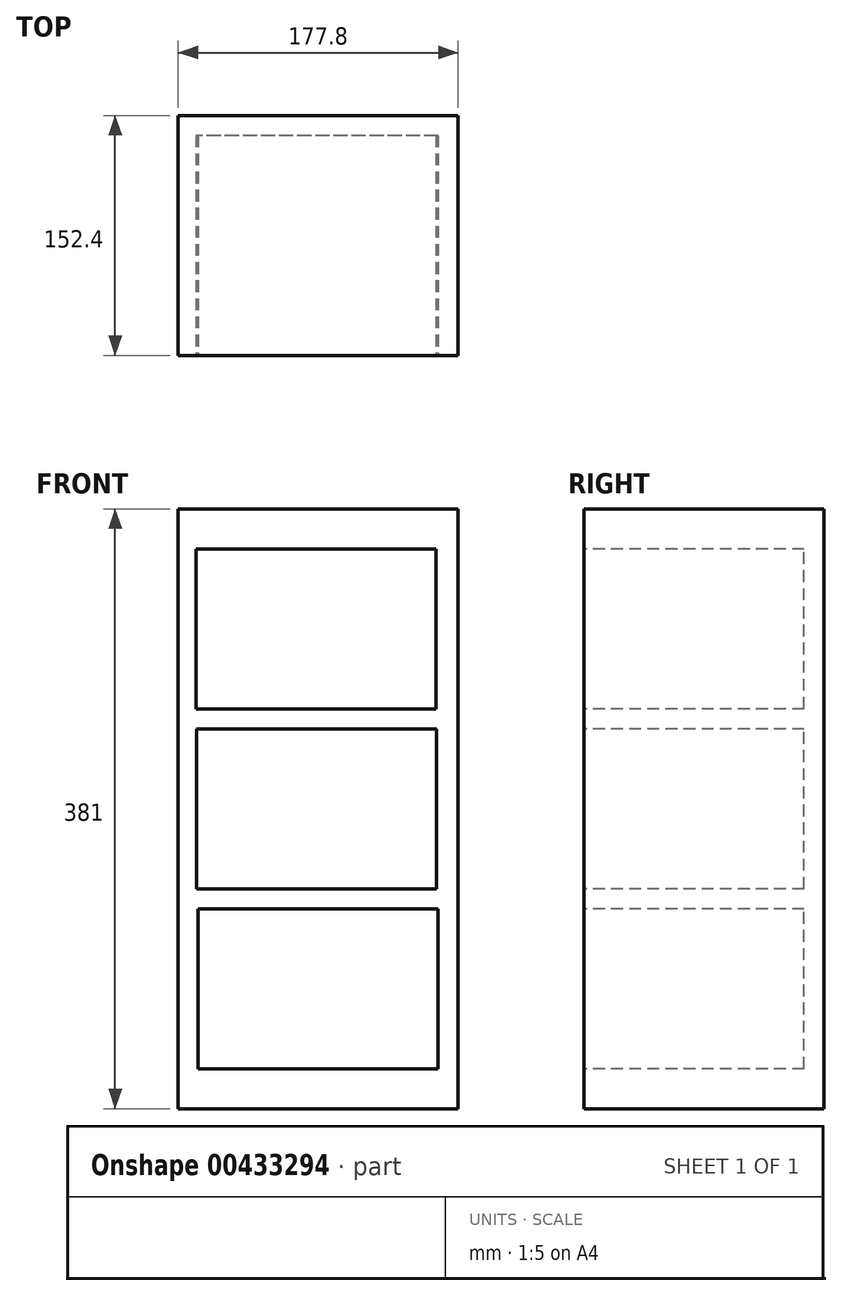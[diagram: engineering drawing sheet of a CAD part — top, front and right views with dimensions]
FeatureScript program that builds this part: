
annotation { "Feature Type Name" : "Feature", "Feature Type Description" : "" }
export const myFeature = defineFeature(function(context is Context, id is Id, definition is map)
    precondition{}
    {
        {
            var Q0;
            Q0=qCreatedBy(makeId("Top.planeOp"),FACE);
            var sketch = newSketch(context, id + "F0", { "sketchPlane" : qUnion([Q0])});
            skLineSegment(sketch, "E0.bottom", {"start": v(88.9, -76.2) * mm, "end": v(-88.9, -76.2) * mm});
            skLineSegment(sketch, "E0.top", {"start": v(88.9, 76.2) * mm, "end": v(-88.9, 76.2) * mm});
            skLineSegment(sketch, "E0.left", {"start": v(88.9, -76.2) * mm, "end": v(88.9, 76.2) * mm});
            skLineSegment(sketch, "E0.right", {"start": v(-88.9, -76.2) * mm, "end": v(-88.9, 76.2) * mm});
            skPoint(sketch, "E0.middle", {"position": v(0, 0) * mm});
            skSolve(sketch);
        }
        {
            var Q0;
            Q0 = qSketchRegion(id + "F0", true);
            extrude(context, id + "F1", {"entities" : qUnion([Q0]), "depth" : 381 * mm});
        }
        {
            var Q0;
            Q0=makeQuery(id+"F1.opExtrude","SWEPT_FACE",FACE,{"disambiguationData":[OSD([sQuery(id+"F0.wireOp",EDGE,"E0.bottom")])]});
            var sketch = newSketch(context, id + "F2", { "sketchPlane" : qUnion([Q0])});
            skLineSegment(sketch, "E1.bottom", {"start": v(74.7, 254) * mm, "end": v(-77.7, 254) * mm});
            skLineSegment(sketch, "E1.top", {"start": v(74.7, 355.6) * mm, "end": v(-77.7, 355.6) * mm});
            skLineSegment(sketch, "E1.left", {"start": v(74.7, 254) * mm, "end": v(74.7, 355.6) * mm});
            skLineSegment(sketch, "E1.right", {"start": v(-77.7, 254) * mm, "end": v(-77.7, 355.6) * mm});
            skPoint(sketch, "E1.middle", {"position": v(-1.5, 304.8) * mm});
            skSolve(sketch);
        }
        {
            var Q0;
            Q0=makeQuery(id+"F2.imprint","IMPRINT",FACE,{"disambiguationData":[TD([[makeQuery(id+"F2.imprint","IMPRINT",EDGE,{"derivedFrom":sQuery(id+"F2.wireOp",EDGE,"E1.bottom")}),-1.0]])]});
            extrude(context, id + "F3", {"entities" : qUnion([Q0]), "operationType" : NewBodyOperationType.REMOVE, "oppositeDirection" : true, "depth" : 139.7 * mm});
        }
        {
            var Q0;
            Q0=makeQuery(id+"F1.opExtrude","SWEPT_FACE",FACE,{"disambiguationData":[OSD([sQuery(id+"F0.wireOp",EDGE,"E0.bottom")])]});
            var sketch = newSketch(context, id + "F4", { "sketchPlane" : qUnion([Q0])});
            skLineSegment(sketch, "E2.bottom", {"start": v(75.1, 139.7) * mm, "end": v(-77.3, 139.7) * mm});
            skLineSegment(sketch, "E2.top", {"start": v(75.1, 241.3) * mm, "end": v(-77.3, 241.3) * mm});
            skLineSegment(sketch, "E2.left", {"start": v(75.1, 139.7) * mm, "end": v(75.1, 241.3) * mm});
            skLineSegment(sketch, "E2.right", {"start": v(-77.3, 139.7) * mm, "end": v(-77.3, 241.3) * mm});
            skPoint(sketch, "E2.middle", {"position": v(-1.1, 190.5) * mm});
            skSolve(sketch);
        }
        {
            var Q0;
            Q0=makeQuery(id+"F4.imprint","IMPRINT",FACE,{"disambiguationData":[TD([[makeQuery(id+"F4.imprint","IMPRINT",EDGE,{"derivedFrom":sQuery(id+"F4.wireOp",EDGE,"E2.bottom")}),1.0]])]});
            var sketch = newSketch(context, id + "F5", { "sketchPlane" : qUnion([Q0])});
            skLineSegment(sketch, "E3.bottom", {"start": v(76.2, 25.4) * mm, "end": v(-76.2, 25.4) * mm});
            skLineSegment(sketch, "E3.top", {"start": v(76.2, 127) * mm, "end": v(-76.2, 127) * mm});
            skLineSegment(sketch, "E3.left", {"start": v(76.2, 25.4) * mm, "end": v(76.2, 127) * mm});
            skLineSegment(sketch, "E3.right", {"start": v(-76.2, 25.4) * mm, "end": v(-76.2, 127) * mm});
            skPoint(sketch, "E3.middle", {"position": v(0, 76.2) * mm});
            skSolve(sketch);
        }
        {
            var Q0;
            Q0=makeQuery(id+"F4.imprint","IMPRINT",FACE,{"disambiguationData":[TD([[makeQuery(id+"F4.imprint","IMPRINT",EDGE,{"derivedFrom":sQuery(id+"F4.wireOp",EDGE,"E2.bottom")}),-1.0]])]});
            extrude(context, id + "F6", {"entities" : qUnion([Q0]), "operationType" : NewBodyOperationType.REMOVE, "oppositeDirection" : true, "depth" : 139.7 * mm});
        }
        {
            var Q0;
            Q0=makeQuery(id+"F5.imprint","IMPRINT",FACE,{"disambiguationData":[TD([[makeQuery(id+"F5.imprint","IMPRINT",EDGE,{"derivedFrom":sQuery(id+"F5.wireOp",EDGE,"E3.bottom")}),-1.0]])]});
            extrude(context, id + "F7", {"entities" : qUnion([Q0]), "operationType" : NewBodyOperationType.REMOVE, "oppositeDirection" : true, "depth" : 139.7 * mm});
        }
    });
